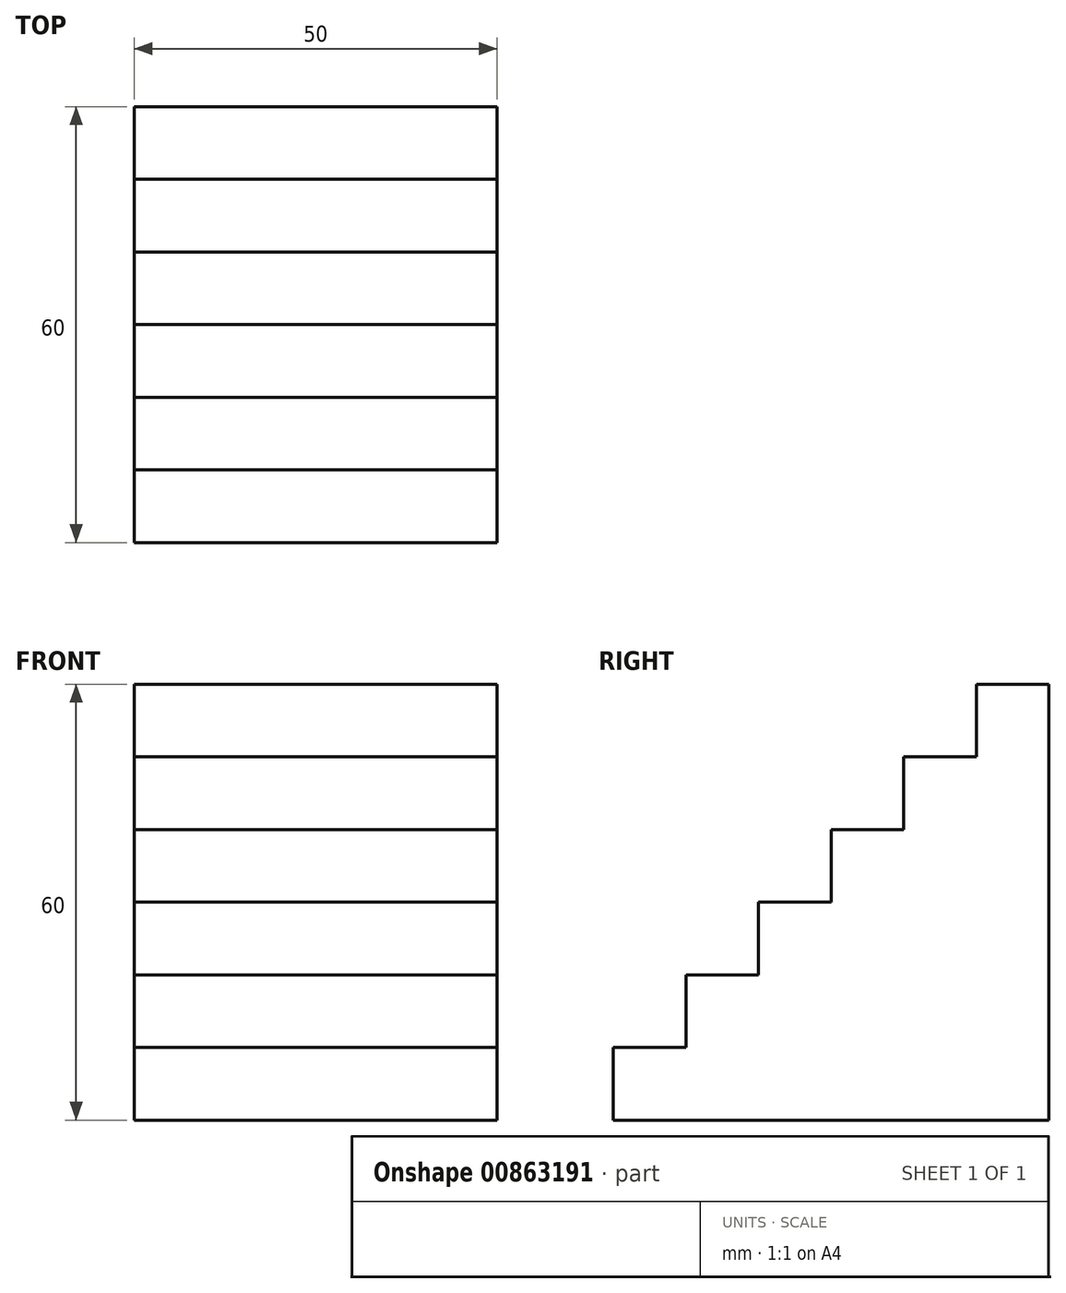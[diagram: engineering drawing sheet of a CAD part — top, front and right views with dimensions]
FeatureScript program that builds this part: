
annotation { "Feature Type Name" : "Feature", "Feature Type Description" : "" }
export const myFeature = defineFeature(function(context is Context, id is Id, definition is map)
    precondition{}
    {
        {
            var Q0;
            Q0=qCreatedBy(makeId("Top.planeOp"),FACE);
            var sketch = newSketch(context, id + "F0", { "sketchPlane" : qUnion([Q0])});
            skLineSegment(sketch, "E0.bottom", {"start": v(25, -5) * mm, "end": v(-25, -5) * mm});
            skLineSegment(sketch, "E0.top", {"start": v(25, 5) * mm, "end": v(-25, 5) * mm});
            skLineSegment(sketch, "E0.left", {"start": v(25, -5) * mm, "end": v(25, 5) * mm});
            skLineSegment(sketch, "E0.right", {"start": v(-25, -5) * mm, "end": v(-25, 5) * mm});
            skPoint(sketch, "E0.middle", {"position": v(0, 0) * mm});
            skSolve(sketch);
        }
        {
            var Q0;
            Q0=makeQuery(id+"F0.imprint","IMPRINT",FACE,{"disambiguationData":[TD([[makeQuery(id+"F0.imprint","IMPRINT",EDGE,{"derivedFrom":sQuery(id+"F0.wireOp",EDGE,"E0.bottom")}),-1.0]])]});
            extrude(context, id + "F1", {"entities" : qUnion([Q0]), "depth" : 60 * mm, "offsetDistance" : 25 * mm});
        }
        {
            var Q0;
            Q0=makeQuery(id+"F1.opExtrude","SWEPT_FACE",FACE,{"disambiguationData":[OSD([sQuery(id+"F0.wireOp",EDGE,"E0.bottom")])]});
            var sketch = newSketch(context, id + "F2", { "sketchPlane" : qUnion([Q0])});
            skLineSegment(sketch, "E1.bottom", {"start": v(-25, 50) * mm, "end": v(25, 50) * mm});
            skLineSegment(sketch, "E1.top", {"start": v(-25, 40) * mm, "end": v(25, 40) * mm});
            skLineSegment(sketch, "E1.left", {"start": v(-25, 50) * mm, "end": v(-25, 40) * mm});
            skLineSegment(sketch, "E1.right", {"start": v(25, 50) * mm, "end": v(25, 40) * mm});
            skSolve(sketch);
        }
        {
            var Q0;
            Q0=makeQuery(id+"F2.imprint","IMPRINT",FACE,{"disambiguationData":[TD([[makeQuery(id+"F2.imprint","IMPRINT",EDGE,{"derivedFrom":sQuery(id+"F2.wireOp",EDGE,"E1.bottom")}),-1.0]])]});
            extrude(context, id + "F3", {"entities" : qUnion([Q0]), "operationType" : NewBodyOperationType.ADD, "depth" : 10 * mm, "offsetDistance" : 25 * mm});
        }
        {
            var Q0;
            {var subQ2=sQuery(id+"F0.wireOp",EDGE,"E0.bottom");Q0=makeQuery(id+"F3.boolean.opBoolean","SPLIT",FACE,{"disambiguationData":[TD([makeQuery(id+"F3.opExtrude","SWEPT_FACE",FACE,{"disambiguationData":[OSD([sQuery(id+"F2.wireOp",EDGE,"E1.top")])]})])],"derivedFrom":makeQuery(id+"F1.opExtrude","SWEPT_FACE",FACE,{"disambiguationData":[OSD([subQ2])]})});}
            var sketch = newSketch(context, id + "F4", { "sketchPlane" : qUnion([Q0])});
            skLineSegment(sketch, "E2.bottom", {"start": v(-25, 40) * mm, "end": v(25, 40) * mm});
            skLineSegment(sketch, "E2.top", {"start": v(-25, 30) * mm, "end": v(25, 30) * mm});
            skLineSegment(sketch, "E2.left", {"start": v(-25, 40) * mm, "end": v(-25, 30) * mm});
            skLineSegment(sketch, "E2.right", {"start": v(25, 40) * mm, "end": v(25, 30) * mm});
            skSolve(sketch);
        }
        {
            var Q0;
            Q0=makeQuery(id+"F4.imprint","IMPRINT",FACE,{"disambiguationData":[TD([[makeQuery(id+"F4.imprint","IMPRINT",EDGE,{"derivedFrom":sQuery(id+"F4.wireOp",EDGE,"E2.bottom")}),-1.0]])]});
            extrude(context, id + "F5", {"entities" : qUnion([Q0]), "operationType" : NewBodyOperationType.ADD, "depth" : 20 * mm, "offsetDistance" : 25 * mm});
        }
        {
            var Q0;
            {var subQ2=sQuery(id+"F0.wireOp",EDGE,"E0.bottom");Q0=makeQuery(id+"F3.boolean.opBoolean","SPLIT",FACE,{"disambiguationData":[TD([makeQuery(id+"F3.opExtrude","SWEPT_FACE",FACE,{"disambiguationData":[OSD([sQuery(id+"F2.wireOp",EDGE,"E1.top")])]})])],"derivedFrom":makeQuery(id+"F1.opExtrude","SWEPT_FACE",FACE,{"disambiguationData":[OSD([subQ2])]})});}
            var sketch = newSketch(context, id + "F6", { "sketchPlane" : qUnion([Q0])});
            skLineSegment(sketch, "E3.bottom", {"start": v(-25, 30) * mm, "end": v(25, 30) * mm});
            skLineSegment(sketch, "E3.top", {"start": v(-25, 20) * mm, "end": v(25, 20) * mm});
            skLineSegment(sketch, "E3.left", {"start": v(-25, 30) * mm, "end": v(-25, 20) * mm});
            skLineSegment(sketch, "E3.right", {"start": v(25, 30) * mm, "end": v(25, 20) * mm});
            skSolve(sketch);
        }
        {
            var Q0;
            Q0=makeQuery(id+"F6.imprint","IMPRINT",FACE,{"disambiguationData":[TD([[makeQuery(id+"F6.imprint","IMPRINT",EDGE,{"derivedFrom":sQuery(id+"F6.wireOp",EDGE,"E3.bottom")}),-1.0]])]});
            extrude(context, id + "F7", {"entities" : qUnion([Q0]), "operationType" : NewBodyOperationType.ADD, "depth" : 30 * mm, "offsetDistance" : 25 * mm});
        }
        {
            var Q0;
            {var subQ2=sQuery(id+"F0.wireOp",EDGE,"E0.bottom");Q0=makeQuery(id+"F3.boolean.opBoolean","SPLIT",FACE,{"disambiguationData":[TD([makeQuery(id+"F3.opExtrude","SWEPT_FACE",FACE,{"disambiguationData":[OSD([sQuery(id+"F2.wireOp",EDGE,"E1.top")])]})])],"derivedFrom":makeQuery(id+"F1.opExtrude","SWEPT_FACE",FACE,{"disambiguationData":[OSD([subQ2])]})});}
            var sketch = newSketch(context, id + "F8", { "sketchPlane" : qUnion([Q0])});
            skLineSegment(sketch, "E4.bottom", {"start": v(-25, 20) * mm, "end": v(25, 20) * mm});
            skLineSegment(sketch, "E4.top", {"start": v(-25, 10) * mm, "end": v(25, 10) * mm});
            skLineSegment(sketch, "E4.left", {"start": v(-25, 20) * mm, "end": v(-25, 10) * mm});
            skLineSegment(sketch, "E4.right", {"start": v(25, 20) * mm, "end": v(25, 10) * mm});
            skSolve(sketch);
        }
        {
            var Q0;
            Q0=makeQuery(id+"F8.imprint","IMPRINT",FACE,{"disambiguationData":[TD([[makeQuery(id+"F8.imprint","IMPRINT",EDGE,{"derivedFrom":sQuery(id+"F8.wireOp",EDGE,"E4.bottom")}),-1.0]])]});
            extrude(context, id + "F9", {"entities" : qUnion([Q0]), "operationType" : NewBodyOperationType.ADD, "depth" : 40 * mm, "offsetDistance" : 25 * mm});
        }
        {
            var Q0;
            {var subQ2=sQuery(id+"F0.wireOp",EDGE,"E0.bottom");Q0=makeQuery(id+"F3.boolean.opBoolean","SPLIT",FACE,{"disambiguationData":[TD([makeQuery(id+"F3.opExtrude","SWEPT_FACE",FACE,{"disambiguationData":[OSD([sQuery(id+"F2.wireOp",EDGE,"E1.top")])]})])],"derivedFrom":makeQuery(id+"F1.opExtrude","SWEPT_FACE",FACE,{"disambiguationData":[OSD([subQ2])]})});}
            var sketch = newSketch(context, id + "F10", { "sketchPlane" : qUnion([Q0])});
            skLineSegment(sketch, "E5.bottom", {"start": v(-25, 10) * mm, "end": v(25, 10) * mm});
            skLineSegment(sketch, "E5.top", {"start": v(-25, 0) * mm, "end": v(25, 0) * mm});
            skLineSegment(sketch, "E5.left", {"start": v(-25, 10) * mm, "end": v(-25, 0) * mm});
            skLineSegment(sketch, "E5.right", {"start": v(25, 10) * mm, "end": v(25, 0) * mm});
            skSolve(sketch);
        }
        {
            var Q0;
            Q0=makeQuery(id+"F10.imprint","IMPRINT",FACE,{"disambiguationData":[TD([[makeQuery(id+"F10.imprint","IMPRINT",EDGE,{"derivedFrom":sQuery(id+"F10.wireOp",EDGE,"E5.bottom")}),-1.0]])]});
            extrude(context, id + "F11", {"entities" : qUnion([Q0]), "operationType" : NewBodyOperationType.ADD, "depth" : 50 * mm, "offsetDistance" : 25 * mm});
        }
    });
